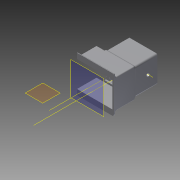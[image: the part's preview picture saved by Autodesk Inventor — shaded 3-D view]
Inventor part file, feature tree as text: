
AUTODESK INVENTOR PART (.ipt)
format: ipt  version: 2012 (Build 160160000, 160)  size: 865,792 bytes
history: native  units: mm
features: sketch x31, extrude x31, reference x30, projected_geometry x23, fillet x12, plane x5, other x3
ambient origin geometry x8: Origin, YZ Plane, XZ Plane, XY Plane, X Axis, Y Axis, Z Axis, Center Point
bodies: Solid1 (feature_tree)
feature tree (135):
  plane  "Work Plane2"
  sketch  "Sketch3"  dims[d1=0.3mm d2=0.3mm]
  plane  "Work Plane3"
  extrude  "Extrusion1"  Depth=0.3mm
  extrude  "Extrusion2"  Depth=10.0mm TaperAngle=0.0deg
  plane  "Work Plane4"
  extrude  "Extrusion3"  Depth=10.0mm TaperAngle=0.0deg
  extrude  "Extrusion4"  Depth=2.0mm
  extrude  "Extrusion5"  Depth=2.0mm
  extrude  "Extrusion6"  Depth=2.0mm TaperAngle=0.0deg
  extrude  "Extrusion7"  TaperAngle=0.0deg  [1 undecoded]
  extrude  "Extrusion8"  TaperAngle=0.0deg  [1 undecoded]
  fillet  "Fillet3"  Radius=20.0mm
  fillet  "Fillet4"  Radius=20.0mm
  fillet  "Fillet5"  Radius=0.3mm
  extrude  "Extrusion10"  Depth=0.3mm
  extrude  "Extrusion11"  Depth=0.3mm TaperAngle=0.0deg
  extrude  "Extrusion12"  Depth=1.0mm
  extrude  "Extrusion13"  Depth=2.0mm TaperAngle=0.0deg
  extrude  "Extrusion14"  Depth=0.3mm
  extrude  "Extrusion15"  Depth=0.3mm
  extrude  "Extrusion16"  TaperAngle=0.0deg  [1 undecoded]
  extrude  "Extrusion17"  Depth=2.0mm
  extrude  "Extrusion18"  Depth=2.0mm TaperAngle=0.0deg
  extrude  "Extrusion20"  Depth=14.0mm
  extrude  "Extrusion21"  Depth=7.0mm TaperAngle=0.0deg
  plane  "Work Plane5"
  extrude  "Extrusion22"  Depth=3.3mm
  extrude  "Extrusion23"  Depth=3.3mm
  extrude  "Extrusion24"  Depth=0.3mm
  extrude  "Extrusion25"  Depth=0.3mm
  plane  "Work Plane7"
  extrude  "Extrusion26"  Depth=20.0mm TaperAngle=0.0deg
  extrude  "Extrusion27"  Depth=0.3mm
  extrude  "Extrusion28"  Depth=0.3mm
  extrude  "Extrusion29"  Depth=2.0mm
  extrude  "Extrusion30"  Depth=2.0mm
  extrude  "Extrusion31"  TaperAngle=45.0deg  [1 undecoded]
  extrude  "Extrusion34"  Depth=9.0mm
  other  "Work Axis1"
  other  "Work Axis2"
  fillet  "Fillet47"  Radius=10.0mm
  fillet  "Fillet48"  [1 undecoded]
  fillet  "Fillet49"  Radius=10.0mm
  fillet  "Fillet50"  Radius=10.0mm
  fillet  "Fillet51"  Radius=10.0mm
  fillet  "Fillet52"  Radius=0.3mm
  fillet  "Fillet53"  Radius=0.3mm
  fillet  "Fillet54"  Radius=10.0mm
  fillet  "Fillet55"  Radius=10.0mm
  other  "Work Axis3"
  extrude  "Extrusion35"  Depth=4.0mm
  reference  "Reference32"
  sketch  "Sketch4"  dims[d3=2.0mm d4=10.0mm d5=0.0mm]
  reference  "Reference33"
  sketch  "Sketch5"  dims[d6=0.3mm d7=10.0mm d8=0.0mm]
  sketch  "Sketch7"  dims[d9=2.0mm d10=2.0mm]
  projected_geometry  "Projected Loop3"
  sketch  "Sketch8"  dims[d11=2.0mm d12=2.0mm]
  sketch  "Sketch10"  dims[d13=120.0mm d14=2.0mm d15=0.0mm]
  reference  "Reference36"
  sketch  "Sketch11"  dims[d24=2.0mm d25=0.0mm]
  reference  "Reference37"
  sketch  "Sketch12"  dims[d26=2.0mm d27=0.0mm d28=20.0mm d29=0.0mm d31=20.0mm d32=0.0mm d34=0.3mm]
  sketch  "Sketch15"  dims[d35=20.0mm d36=0.0mm d37=0.3mm]
  projected_geometry  "Projected Loop5"
  projected_geometry  "Projected Loop6"
  sketch  "Sketch16"  dims[d38=10.0mm d39=0.0mm d40=0.3mm d41=0.0mm]
  reference  "Reference46"
  reference  "Reference47"
  reference  "Reference48"
  reference  "Reference49"
  reference  "Reference50"
  reference  "Reference51"
  reference  "Reference52"
  reference  "Reference53"
  sketch  "Sketch17"  dims[d43=1.0mm d44=1.0mm]
  reference  "Reference54"
  reference  "Reference55"
  reference  "Reference56"
  reference  "Reference57"
  reference  "Reference58"
  reference  "Reference59"
  reference  "Reference60"
  reference  "Reference61"
  sketch  "Sketch18"  dims[d45=1.0mm d52=2.0mm d53=0.0mm]
  reference  "Reference62"
  sketch  "Sketch19"  dims[d58=2.0mm d59=0.0mm d60=0.3mm]
  projected_geometry  "Projected Loop7"
  projected_geometry  "Projected Loop8"
  sketch  "Sketch20"  dims[d61=0.3mm d62=0.3mm]
  projected_geometry  "Projected Loop9"
  projected_geometry  "Projected Loop10"
  sketch  "Sketch21"  dims[d63=0.3mm d64=0.0mm]
  projected_geometry  "Projected Loop11"
  sketch  "Sketch22"  dims[d66=0.0mm d67=2.0mm]
  reference  "Reference63"
  reference  "Reference64"
  reference  "Reference65"
  reference  "Reference66"
  reference  "Reference67"
  reference  "Reference68"
  reference  "Reference69"
  reference  "Reference70"
  sketch  "Sketch23"  dims[d68=2.0mm d69=2.0mm d70=0.0mm]
  projected_geometry  "Projected Loop12"
  projected_geometry  "Projected Loop13"
  projected_geometry  "Projected Loop14"
  projected_geometry  "Projected Loop15"
  sketch  "Sketch25"  dims[d72=2.0mm d73=0.0mm d74=14.0mm]
  projected_geometry  "Projected Loop16"
  sketch  "Sketch26"  dims[d78=2.0mm d79=0.0mm d80=7.0mm d81=0.0mm]
  sketch  "Sketch28"  dims[d82=10.0mm d83=0.0mm d84=3.3mm]
  projected_geometry  "Projected Loop21"
  sketch  "Sketch29"  dims[d85=3.3mm d86=3.3mm]
  projected_geometry  "Projected Loop22"
  projected_geometry  "Projected Loop23"
  sketch  "Sketch30"  dims[d87=3.3mm d88=0.3mm]
  projected_geometry  "Projected Loop24"
  sketch  "Sketch31"  dims[d89=0.3mm d90=0.3mm]
  projected_geometry  "Projected Loop25"
  sketch  "Sketch32"  dims[d91=0.3mm d94=20.0mm d95=0.0mm]
  sketch  "Sketch33"  dims[d97=0.3mm d98=0.3mm]
  projected_geometry  "Projected Loop26"
  sketch  "Sketch34"  dims[d99=0.3mm d100=0.3mm]
  projected_geometry  "Projected Loop27"
  sketch  "Sketch35"  dims[d101=0.3mm d102=0.0mm d103=2.0mm]
  projected_geometry  "Projected Loop28"
  projected_geometry  "Projected Loop29"
  sketch  "Sketch37"  dims[d104=2.0mm d105=2.0mm]
  sketch  "Sketch38"  dims[d106=2.0mm d111=45.0deg]
  projected_geometry  "Projected Loop31"
  sketch  "Sketch41"  dims[d112=9.0mm d113=9.0mm d114=10.0mm d115=0.0mm d116=0.0mm d117=0.0mm d123=10.0mm d124=0.0mm d132=10.0mm d133=0.0mm d134=10.0mm d135=0.0mm d138=0.3mm d139=0.0mm d151=0.3mm d152=0.0mm d153=10.0mm d154=0.0mm d155=10.0mm d156=0.0mm]
  reference  "Reference73"
  sketch  "Sketch42"  dims[d157=10.0mm d158=0.0mm d159=4.0mm d160=10.0mm d161=0.0mm d162=10.0mm d163=0.0mm d186=25.4mm d187=0.0mm d189=1.0mm d190=2.0mm d191=2.0mm d192=2.0mm d193=2.0mm d194=1.0mm d195=2.0mm d196=2.0mm d197=1.5mm d198=0.0mm d199=0.0mm]
note: 5 required parameter values undecoded (feature->parameter linkage not recoverable at this tier; creation-order binding heuristic only, values carry confidence <= 0.55)
